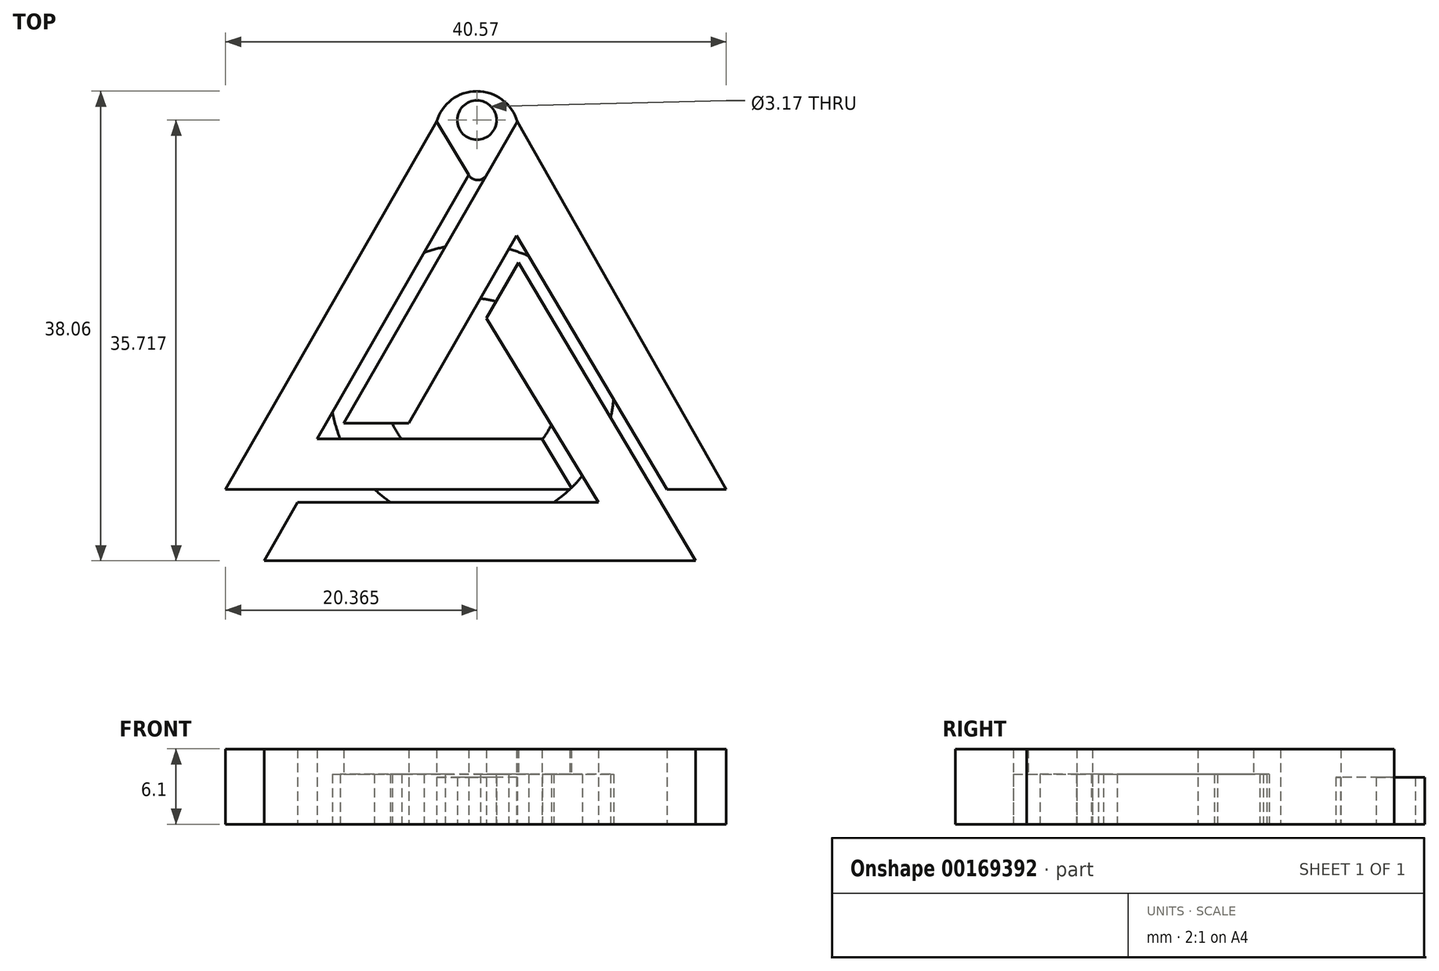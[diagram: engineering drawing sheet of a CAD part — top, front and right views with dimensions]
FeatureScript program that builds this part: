
annotation { "Feature Type Name" : "Feature", "Feature Type Description" : "" }
export const myFeature = defineFeature(function(context is Context, id is Id, definition is map)
    precondition{}
    {
        {
            var Q0;
            Q0=qCreatedBy(makeId("Top.planeOp"),FACE);
            var sketch = newSketch(context, id + "F0", { "sketchPlane" : qUnion([Q0])});
            skLineSegment(sketch, "E0", {"start": v(-4.05, 16.82) * mm, "end": v(-21.14, -12.98) * mm});
            skLineSegment(sketch, "E1", {"start": v(-21.14, -12.98) * mm, "end": v(6.97, -12.98) * mm});
            skLineSegment(sketch, "E2", {"start": v(6.97, -12.98) * mm, "end": v(4.5, -8.9) * mm});
            skLineSegment(sketch, "E3", {"start": v(4.5, -8.9) * mm, "end": v(-13.72, -8.9) * mm});
            skLineSegment(sketch, "E4", {"start": v(-13.72, -8.9) * mm, "end": v(-1.44, 12.5) * mm});
            skLineSegment(sketch, "E5", {"start": v(-4.05, 16.82) * mm, "end": v(-1.44, 12.5) * mm});
            skLineSegment(sketch, "E6", {"start": v(-11.56, -7.63) * mm, "end": v(-6.29, -7.63) * mm});
            skLineSegment(sketch, "E7", {"start": v(-6.29, -7.63) * mm, "end": v(2.45, 7.6) * mm});
            skLineSegment(sketch, "E8", {"start": v(2.45, 7.6) * mm, "end": v(14.64, -12.98) * mm});
            skLineSegment(sketch, "E9", {"start": v(14.64, -12.98) * mm, "end": v(19.43, -12.98) * mm});
            skLineSegment(sketch, "E10", {"start": v(19.43, -12.98) * mm, "end": v(2.5, 16.82) * mm});
            skLineSegment(sketch, "E11", {"start": v(2.5, 16.82) * mm, "end": v(-11.56, -7.63) * mm});
            skLineSegment(sketch, "E12", {"start": v(2.58, 5.4) * mm, "end": v(0, 0.9) * mm});
            skLineSegment(sketch, "E13", {"start": v(0, 0.9) * mm, "end": v(9.08, -14.04) * mm});
            skLineSegment(sketch, "E14", {"start": v(9.08, -14.04) * mm, "end": v(-15.31, -14.04) * mm});
            skLineSegment(sketch, "E15", {"start": v(-15.31, -14.04) * mm, "end": v(-18.02, -18.77) * mm});
            skLineSegment(sketch, "E16", {"start": v(-18.02, -18.77) * mm, "end": v(16.96, -18.77) * mm});
            skLineSegment(sketch, "E17", {"start": v(16.96, -18.77) * mm, "end": v(2.58, 5.4) * mm});
            skArc(sketch, "E18", {"start": v(-12.48, -6.74) * mm, "mid": v(-12.21, -7.84) * mm, "end": v(-11.85, -8.9) * mm});
            skArc(sketch, "E19", {"start": v(0.77, 2.25) * mm, "mid": v(0.15, 2.4) * mm, "end": v(-0.49, 2.48) * mm});
            skArc(sketch, "E20.trimOffspring", {"start": v(-3.33, 6.68) * mm, "mid": v(-4.2, 6.47) * mm, "end": v(-5.05, 6.2) * mm});
            skArc(sketch, "E21.trimOffspring", {"start": v(3.44, 5.92) * mm, "mid": v(2.64, 6.24) * mm, "end": v(1.81, 6.5) * mm});
            skArc(sketch, "E22.trimOffspring", {"start": v(-7.64, -7.63) * mm, "mid": v(-7.3, -8.29) * mm, "end": v(-6.88, -8.9) * mm});
            skArc(sketch, "E23.trimOffspring", {"start": v(4.52, -8.95) * mm, "mid": v(4.92, -8.37) * mm, "end": v(5.26, -7.75) * mm});
            skArc(sketch, "E24.trimOffspring", {"start": v(-9.08, -12.98) * mm, "mid": v(-8.45, -13.53) * mm, "end": v(-7.78, -14.04) * mm});
            skArc(sketch, "E25.trimOffspring", {"start": v(5.45, -14.04) * mm, "mid": v(6.69, -13.04) * mm, "end": v(7.77, -11.89) * mm});
            skArc(sketch, "E26.trimOffspring", {"start": v(10.06, -7.18) * mm, "mid": v(10.2, -6.42) * mm, "end": v(10.3, -5.66) * mm});
            skArc(sketch, "E27", {"start": v(2.5, 16.82) * mm, "mid": v(-0.77, 19.29) * mm, "end": v(-4.05, 16.82) * mm});
            skCircle(sketch, "E28", {"center": v(-0.77, 16.95) * mm, "radius": 1.59 * mm});
            skArc(sketch, "E29", {"start": v(-1.44, 12.5) * mm, "mid": v(-0.73, 12.08) * mm, "end": v(0, 12.47) * mm});
            skSolve(sketch);
        }
        {
            var Q0;
            {var subQ4=sQuery(id+"F0.wireOp",EDGE,"E18");Q0=makeQuery(id+"F0.imprint","IMPRINT",FACE,{"disambiguationData":[TD([[makeQuery(id+"F0.imprint","IMPRINT",EDGE,{"derivedFrom":subQ4}),1.0]])]});}
            var Q1;
            {var subQ3=sQuery(id+"F0.wireOp",EDGE,"E19");Q1=makeQuery(id+"F0.imprint","IMPRINT",FACE,{"disambiguationData":[TD([[makeQuery(id+"F0.imprint","IMPRINT",EDGE,{"derivedFrom":subQ3}),-1.0]])]});}
            var Q2;
            {var subQ0=sQuery(id+"F0.wireOp",EDGE,"E23.trimOffspring");Q2=makeQuery(id+"F0.imprint","IMPRINT",FACE,{"disambiguationData":[TD([[makeQuery(id+"F0.imprint","IMPRINT",EDGE,{"derivedFrom":subQ0}),-1.0]])]});}
            var Q3;
            {var subQ0=sQuery(id+"F0.wireOp",EDGE,"E24.trimOffspring");Q3=makeQuery(id+"F0.imprint","IMPRINT",FACE,{"disambiguationData":[TD([[makeQuery(id+"F0.imprint","IMPRINT",EDGE,{"derivedFrom":subQ0}),1.0]])]});}
            extrude(context, id + "F1", {"entities" : qUnion([Q0, Q1, Q2, Q3]), "depth" : 4.06 * mm});
        }
        {
            var Q0;
            {var subQ9=sQuery(id+"F0.wireOp",EDGE,"E0");Q0=makeQuery(id+"F0.imprint","IMPRINT",FACE,{"disambiguationData":[TD([[makeQuery(id+"F0.imprint","IMPRINT",EDGE,{"derivedFrom":subQ9}),1.0]])]});}
            var Q1;
            {var subQ4=sQuery(id+"F0.wireOp",EDGE,"E9");Q1=makeQuery(id+"F0.imprint","IMPRINT",FACE,{"disambiguationData":[TD([[makeQuery(id+"F0.imprint","IMPRINT",EDGE,{"derivedFrom":subQ4}),1.0]])]});}
            var Q2;
            {var subQ5=sQuery(id+"F0.wireOp",EDGE,"E15");Q2=makeQuery(id+"F0.imprint","IMPRINT",FACE,{"disambiguationData":[TD([[makeQuery(id+"F0.imprint","IMPRINT",EDGE,{"derivedFrom":subQ5}),1.0]])]});}
            extrude(context, id + "F2", {"entities" : qUnion([Q0, Q1, Q2]), "operationType" : NewBodyOperationType.ADD, "depth" : 6.1 * mm});
        }
        {
            var Q0;
            Q0=makeQuery(id+"F0.imprint","IMPRINT",FACE,{"disambiguationData":[TD([[makeQuery(id+"F0.imprint","IMPRINT",EDGE,{"derivedFrom":sQuery(id+"F0.wireOp",EDGE,"E5")}),1.0]])]});
            extrude(context, id + "F3", {"entities" : qUnion([Q0]), "operationType" : NewBodyOperationType.ADD, "depth" : 3.8 * mm});
        }
    });
